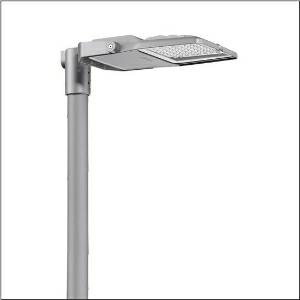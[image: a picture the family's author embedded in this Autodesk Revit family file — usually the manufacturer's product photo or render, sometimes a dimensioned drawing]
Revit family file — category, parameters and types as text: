
# Revit family: floodlight_fl_21_iq_mini___pl33t_5xa7771c2f3a_7d89
name_source: partatom
category: Lighting Fixtures
units: mm (PartAtom-declared; Revit-internal decimal feet)

## family parameters
Cut with Voids When Loaded = No
Host = Face
Light Source = No
Part Type = Normal
Room Calculation Point = No
Round Connector Dimension = Use Diameter
Shared = No

## types (1)
- --- (1 x LED, 12060 lm, 87.2 W, 3000K)
    Apparent Load = 87 VA
    CIE Flux Codes = 26 75 99 100 100
    Color Rendering = 70
    Color Temperature = 3000K
    Default Elevation = 1800 mm
    Description = Floodlight FL 21 iQ mini, floodlight, primary light control with lens, of PMMA, primary optical cover: protective disc, of toughened safety glass, transparent, light distribution: PL33T, light emission: direct distribution, installation type: surface-mounted, LED, High Power LED, rated luminous flux: 12.060lm, luminous efficacy: 138lm/W, light colour: 730, colour temperature: 3000K, control gear: iQ Comfort/DALI, control: Auto-Match, Temp-Guard, Lumen-Switch, Night-Set, Smart-Wire, Light-Fading, Desk-Remote (wireless, voltage-free reading and setting of iQ features in the workshop via application-optimized NFC function/RFID function), optimised constant luminous flux control (CLO 2.0), with terminal, 6-pole, mains connection: 220..240V, AC, 50/60Hz, start of lifetime: 87W, end of service life: 92W, reduction: 40W, luminaire housing, of diecast aluminium, powder-coated, Siteco® metallic grey (DB 702S), corrosivity category C5 mid according to DIN EN ISO 12944, suitable for swimming pools, chlorine-resistant, sealing non-destructively replaceable, please order mast flange separately, mast bracket, of steel, galvanised, powder-coated, Siteco® metallic grey (DB 702S), protection rating (complete): IP66, insulation class (complete): insulation class II (safety insulation), certification: CE, ENEC, VDE, protection symbol: D, impact resistance: IK08, permissible operating ambient temperature: -40..+40°C, permissible operating ambient temperature for outdoor applications: -40..+50°C, standard: DIN EN 12944, LABS conformity tested according to VDMA 24364:2018-05, packaging unit: 1 piece

Light Distribution: PL33T
    Height = 70 mm
    Lamp = 1 x LED
    Lamp Light Flux = 12060 lm
    Lamp Power = 87.2 W
    Lamp count = 1
    Length = 485 mm
    Luminous efficacy = 138 lm/W
    Manufacturer = Siteco
    ModVariant = No
    Model = 5XA7771C2F3A
    Number of Poles = 1
    OnlyDefault = Yes
    Power Factor = 1
    Product Name = Floodlight FL 21 iQ mini | PL33T
    Product group = floodlight | pylon annexe
    ProductGroupID = 6201
    Protection Class = Protection class II
    Protection Degree = IP 66
    RLX_Detail_Level = 1
    RLX_Emergency_Light_Flux = 0 lm
    RLX_Emergency_Type = 0
    RLX_Emergency_Type_DB = No
    RlxData = <blob elided: 101309 chars, md5=ae409b64>
    Socket = socket
    Standby Power = 0 W
    System Light Flux = 12060 lm
    System Power = 87 W
    Type Comments = factory setting: luminous flux: 100 % | dim-lin: 254 | 456 mA
    Type Image = l_1007125.jpg
    URL = http://relux.com
    VarID = @adj_171185
    Voltage = 0 V
    Weight = 0.00 kg
    Width = 337 mm

## geometry (parser evidence)
native form markers: Blend x4, Sweep x16
no freeform markers — native parametric forms only
